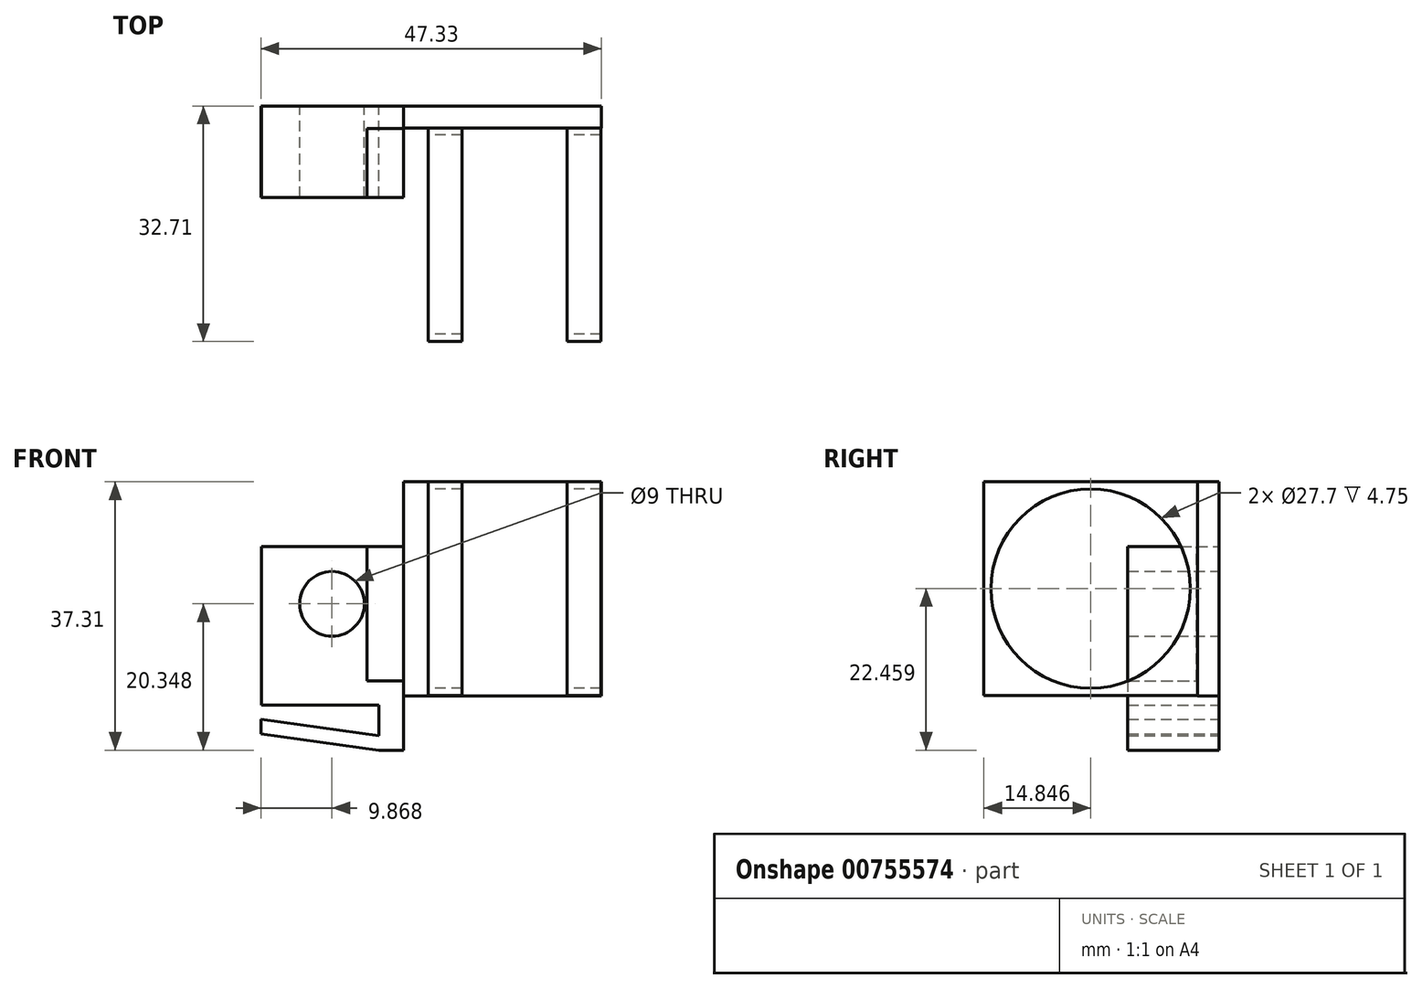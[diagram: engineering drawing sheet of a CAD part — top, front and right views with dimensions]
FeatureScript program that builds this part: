
annotation { "Feature Type Name" : "Feature", "Feature Type Description" : "" }
export const myFeature = defineFeature(function(context is Context, id is Id, definition is map)
    precondition{}
    {
        {
            var Q0;
            Q0=qCreatedBy(makeId("Front.planeOp"),FACE);
            var sketch = newSketch(context, id + "F0", { "sketchPlane" : qUnion([Q0])});
            skLineSegment(sketch, "E0", {"start": v(-23.5, 10.17) * mm, "end": v(-7.1, 7.87) * mm});
            skLineSegment(sketch, "E1", {"start": v(-7.1, 7.87) * mm, "end": v(-7.1, 5.87) * mm});
            skLineSegment(sketch, "E2", {"start": v(-7.1, 5.87) * mm, "end": v(-23.5, 8.17) * mm});
            skLineSegment(sketch, "E3", {"start": v(-23.5, 8.17) * mm, "end": v(-23.5, 10.17) * mm});
            skLineSegment(sketch, "E4", {"start": v(-7.1, 5.87) * mm, "end": v(-3.67, 5.87) * mm});
            skLineSegment(sketch, "E5", {"start": v(-3.67, 5.87) * mm, "end": v(-3.67, 12.17) * mm});
            skLineSegment(sketch, "E6", {"start": v(-3.67, 12.17) * mm, "end": v(-23.46, 12.17) * mm});
            skLineSegment(sketch, "E7", {"start": v(-7.1, 7.87) * mm, "end": v(-7.1, 12.17) * mm});
            skLineSegment(sketch, "E8", {"start": v(-23.46, 12.17) * mm, "end": v(-23.46, 34.2) * mm});
            skLineSegment(sketch, "E9", {"start": v(-23.46, 34.2) * mm, "end": v(-3.67, 34.2) * mm});
            skLineSegment(sketch, "E10", {"start": v(-3.67, 34.2) * mm, "end": v(-3.67, 12.17) * mm});
            skCircle(sketch, "E11", {"center": v(-13.63, 26.22) * mm, "radius": 4.5 * mm});
            skLineSegment(sketch, "E12.top", {"start": v(-3.67, 43.17) * mm, "end": v(23.83, 43.17) * mm});
            skLineSegment(sketch, "E12.left", {"start": v(-3.67, 12.17) * mm, "end": v(-3.67, 43.17) * mm});
            skLineSegment(sketch, "E13", {"start": v(23.83, 43.17) * mm, "end": v(23.83, 13.44) * mm});
            skLineSegment(sketch, "E14", {"start": v(23.83, 13.44) * mm, "end": v(-3.67, 13.44) * mm});
            skLineSegment(sketch, "E15", {"start": v(-3.67, 13.44) * mm, "end": v(-3.67, 43.17) * mm});
            skSolve(sketch);
        }
        {
            var Q0;
            {var subQ0=sQuery(id+"F0.wireOp",EDGE,"E8");Q0=makeQuery(id+"F0.imprint","IMPRINT",FACE,{"disambiguationData":[TD([[makeQuery(id+"F0.imprint","IMPRINT",EDGE,{"derivedFrom":subQ0}),-1.0]])]});}
            var Q1;
            Q1=makeQuery(id+"F0.imprint","IMPRINT",FACE,{"disambiguationData":[TD([[makeQuery(id+"F0.imprint","IMPRINT",EDGE,{"derivedFrom":sQuery(id+"F0.wireOp",EDGE,"E1")}),1.0]])]});
            var Q2;
            Q2=makeQuery(id+"F0.imprint","IMPRINT",FACE,{"disambiguationData":[TD([[makeQuery(id+"F0.imprint","IMPRINT",EDGE,{"derivedFrom":sQuery(id+"F0.wireOp",EDGE,"E0")}),-1.0]])]});
            extrude(context, id + "F1", {"entities" : qUnion([Q0, Q1, Q2]), "depth" : 12.7 * mm, "offsetDistance" : 25.4 * mm});
        }
        {
            var Q0;
            Q0=qCreatedBy(makeId("Right.planeOp"),FACE);
            var sketch = newSketch(context, id + "F2", { "sketchPlane" : qUnion([Q0])});
            skCircle(sketch, "E16", {"center": v(-17.86, 28.33) * mm, "radius": 13.85 * mm});
            skLineSegment(sketch, "E17.bottom", {"start": v(-32.71, 13.48) * mm, "end": v(-3.01, 13.48) * mm});
            skLineSegment(sketch, "E17.top", {"start": v(-32.71, 43.18) * mm, "end": v(-3.01, 43.18) * mm});
            skLineSegment(sketch, "E17.left", {"start": v(-32.71, 13.48) * mm, "end": v(-32.71, 43.18) * mm});
            skLineSegment(sketch, "E17.right", {"start": v(-3.01, 13.48) * mm, "end": v(-3.01, 43.18) * mm});
            skSolve(sketch);
        }
        {
            var Q0;
            Q0=makeQuery(id+"F2.imprint","IMPRINT",FACE,{"disambiguationData":[TD([[makeQuery(id+"F2.imprint","IMPRINT",EDGE,{"derivedFrom":sQuery(id+"F2.wireOp",EDGE,"E16")}),-1.0]])]});
            extrude(context, id + "F3", {"entities" : qUnion([Q0]), "depth" : 0.97 * mm, "offsetDistance" : 25.4 * mm, "hasSecondDirection" : true, "secondDirectionOppositeDirection" : true, "secondDirectionDepth" : 3.78 * mm});
        }
        {
            var Q0;
            Q0=makeQuery(id+"F3.opExtrude","SWEPT_BODY",BODY,{"disambiguationData":[OSD([sQuery(id+"F2.wireOp",EDGE,"E16"),sQuery(id+"F2.wireOp",EDGE,"4rD1Hq7w-VWJ7-KVrg-Awg5-MDBKJ0o3157S.bottom"),sQuery(id+"F2.wireOp",EDGE,"4rD1Hq7w-VWJ7-KVrg-Awg5-MDBKJ0o3157S.left")])]});
            var Q1;
            Q1=makeQuery(id+"Fa8omzMjshyL3zN_1.opExtrude","SWEPT_BODY",BODY,{"disambiguationData":[OSD([sQuery(id+"F0.wireOp",EDGE,"E9"),sQuery(id+"F0.wireOp",EDGE,"E10"),sQuery(id+"F0.wireOp",EDGE,"f65KALD1-Up1J-8yhH-euTF-ZpfFo1jZM9dm"),sQuery(id+"F0.wireOp",EDGE,"YPzdGTZk-8tMm-PfUU-9LoM-J6pCHLWc6F5Q"),sQuery(id+"F0.wireOp",EDGE,"9pe88sZB-isaz-iqt9-vYYI-wqlZmSG8yaND.bottom"),sQuery(id+"F0.wireOp",EDGE,"YF0FOWLr-dner-qBg2-0HDQ-xWlQKmYCPwrV.bottom")])]});
            var Q2;
            Q2=makeQuery(id+"F3.opExtrude","SWEPT_BODY",BODY,{"disambiguationData":[OSD([sQuery(id+"F2.wireOp",EDGE,"E16"),sQuery(id+"F2.wireOp",EDGE,"4rD1Hq7w-VWJ7-KVrg-Awg5-MDBKJ0o3157S.bottom"),sQuery(id+"F2.wireOp",EDGE,"4rD1Hq7w-VWJ7-KVrg-Awg5-MDBKJ0o3157S.right")])]});
            var Q3;
            Q3=makeQuery(id+"F3.opExtrude","SWEPT_BODY",BODY,{"disambiguationData":[OSD([sQuery(id+"F2.wireOp",EDGE,"E16"),sQuery(id+"F2.wireOp",EDGE,"4rD1Hq7w-VWJ7-KVrg-Awg5-MDBKJ0o3157S.top"),sQuery(id+"F2.wireOp",EDGE,"4rD1Hq7w-VWJ7-KVrg-Awg5-MDBKJ0o3157S.left")])]});
            var Q4;
            Q4=makeQuery(id+"F3.opExtrude","SWEPT_BODY",BODY,{"disambiguationData":[OSD([sQuery(id+"F2.wireOp",EDGE,"E16"),sQuery(id+"F2.wireOp",EDGE,"4rD1Hq7w-VWJ7-KVrg-Awg5-MDBKJ0o3157S.top"),sQuery(id+"F2.wireOp",EDGE,"4rD1Hq7w-VWJ7-KVrg-Awg5-MDBKJ0o3157S.right")])]});
            transform(context, id + "F4", {"entities" : qUnion([Q0, Q1, Q2, Q3, Q4]), "transformType" : TransformType.TRANSLATION_3D, "dx" : 3.5 * mm, "dy" : 0 * mm, "dz" : 0 * mm, "makeCopy" : false});
        }
        {
            var Q0;
            Q0=makeQuery(id+"Fa8omzMjshyL3zN_1.opExtrude","SWEPT_BODY",BODY,{"disambiguationData":[OSD([sQuery(id+"F0.wireOp",EDGE,"E9"),sQuery(id+"F0.wireOp",EDGE,"E10"),sQuery(id+"F0.wireOp",EDGE,"f65KALD1-Up1J-8yhH-euTF-ZpfFo1jZM9dm"),sQuery(id+"F0.wireOp",EDGE,"YPzdGTZk-8tMm-PfUU-9LoM-J6pCHLWc6F5Q"),sQuery(id+"F0.wireOp",EDGE,"9pe88sZB-isaz-iqt9-vYYI-wqlZmSG8yaND.bottom"),sQuery(id+"F0.wireOp",EDGE,"YF0FOWLr-dner-qBg2-0HDQ-xWlQKmYCPwrV.bottom")])]});
            var Q1;
            Q1=makeQuery(id+"F3.opExtrude","SWEPT_BODY",BODY,{"disambiguationData":[OSD([sQuery(id+"F2.wireOp",EDGE,"E16"),sQuery(id+"F2.wireOp",EDGE,"4rD1Hq7w-VWJ7-KVrg-Awg5-MDBKJ0o3157S.bottom"),sQuery(id+"F2.wireOp",EDGE,"4rD1Hq7w-VWJ7-KVrg-Awg5-MDBKJ0o3157S.right")])]});
            var Q2;
            Q2=makeQuery(id+"F3.opExtrude","SWEPT_BODY",BODY,{"disambiguationData":[OSD([sQuery(id+"F2.wireOp",EDGE,"E16"),sQuery(id+"F2.wireOp",EDGE,"4rD1Hq7w-VWJ7-KVrg-Awg5-MDBKJ0o3157S.bottom"),sQuery(id+"F2.wireOp",EDGE,"4rD1Hq7w-VWJ7-KVrg-Awg5-MDBKJ0o3157S.left")])]});
            var Q3;
            Q3=makeQuery(id+"F3.opExtrude","SWEPT_BODY",BODY,{"disambiguationData":[OSD([sQuery(id+"F2.wireOp",EDGE,"E16"),sQuery(id+"F2.wireOp",EDGE,"4rD1Hq7w-VWJ7-KVrg-Awg5-MDBKJ0o3157S.top"),sQuery(id+"F2.wireOp",EDGE,"4rD1Hq7w-VWJ7-KVrg-Awg5-MDBKJ0o3157S.left")])]});
            var Q4;
            Q4=makeQuery(id+"F3.opExtrude","SWEPT_BODY",BODY,{"disambiguationData":[OSD([sQuery(id+"F2.wireOp",EDGE,"E16"),sQuery(id+"F2.wireOp",EDGE,"4rD1Hq7w-VWJ7-KVrg-Awg5-MDBKJ0o3157S.top"),sQuery(id+"F2.wireOp",EDGE,"4rD1Hq7w-VWJ7-KVrg-Awg5-MDBKJ0o3157S.right")])]});
            transform(context, id + "F5", {"entities" : qUnion([Q0, Q1, Q2, Q3, Q4]), "transformType" : TransformType.TRANSLATION_3D, "dx" : 19.3 * mm, "dy" : 0 * mm, "dz" : 0 * mm, "makeCopy" : true});
        }
        {
            var Q0;
            {var subQ3=sQuery(id+"F0.wireOp",EDGE,"E12.top");Q0=makeQuery(id+"F0.imprint","IMPRINT",FACE,{"disambiguationData":[TD([[makeQuery(id+"F0.imprint","IMPRINT",EDGE,{"derivedFrom":subQ3}),-1.0]])]});}
            var Q1;
            Q1=makeQuery(id+"F5.opPattern","COPY",FACE,{"derivedFrom":makeQuery(id+"F3.opExtrude","SWEPT_FACE",FACE,{"disambiguationData":[OSD([sQuery(id+"F2.wireOp",EDGE,"E17.right")])]}),"instanceName":"1"});
            extrude(context, id + "F6", {"entities" : qUnion([Q0]), "endBound" : BoundingType.UP_TO_SURFACE, "depth" : 0.76 * mm, "endBoundEntityFace" : qUnion([Q1]), "offsetDistance" : 25.4 * mm});
        }
        {
            var Q0;
            Q0=makeQuery(id+"F1.opExtrude","SWEPT_FACE",FACE,{"disambiguationData":[OSD([sQuery(id+"F0.wireOp",EDGE,"E9")])]});
            var sketch = newSketch(context, id + "F7", { "sketchPlane" : qUnion([Q0])});
            skLineSegment(sketch, "E18.bottom", {"start": v(-3.67, -12.7) * mm, "end": v(-8.76, -12.7) * mm});
            skLineSegment(sketch, "E18.top", {"start": v(-3.67, -3.12) * mm, "end": v(-8.76, -3.12) * mm});
            skLineSegment(sketch, "E18.left", {"start": v(-3.67, -12.7) * mm, "end": v(-3.67, -3.12) * mm});
            skLineSegment(sketch, "E18.right", {"start": v(-8.76, -12.7) * mm, "end": v(-8.76, -3.12) * mm});
            skSolve(sketch);
        }
        {
            var Q0;
            Q0=makeQuery(id+"F7.imprint","IMPRINT",FACE,{"disambiguationData":[TD([[makeQuery(id+"F7.imprint","IMPRINT",EDGE,{"derivedFrom":sQuery(id+"F7.wireOp",EDGE,"E18.bottom")}),1.0]])]});
            extrude(context, id + "F8", {"entities" : qUnion([Q0]), "operationType" : NewBodyOperationType.REMOVE, "oppositeDirection" : true, "depth" : 18.67 * mm, "offsetDistance" : 25.4 * mm});
        }
    });
